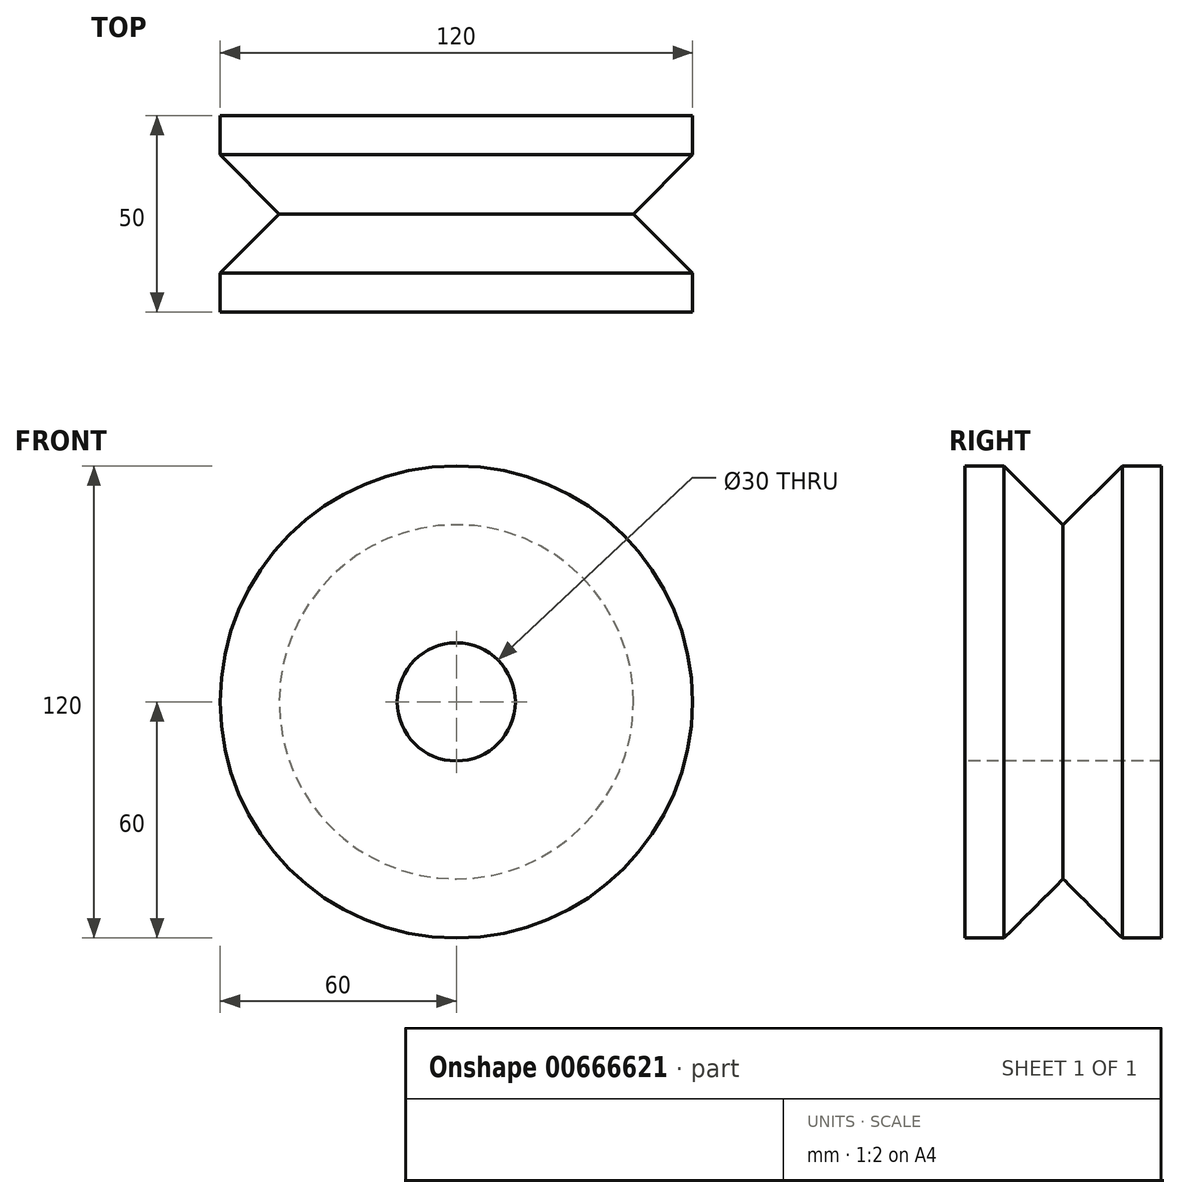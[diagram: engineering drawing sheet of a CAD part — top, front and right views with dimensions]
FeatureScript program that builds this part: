
annotation { "Feature Type Name" : "Feature", "Feature Type Description" : "" }
export const myFeature = defineFeature(function(context is Context, id is Id, definition is map)
    precondition{}
    {
        {
            var Q0;
            Q0=qCreatedBy(makeId("Right.planeOp"),FACE);
            var sketch = newSketch(context, id + "F0", { "sketchPlane" : qUnion([Q0])});
            skPoint(sketch, "E0.middle", {"position": v(0, 0) * mm});
            skLineSegment(sketch, "E1", {"start": v(0, 0) * mm, "end": v(15, 15) * mm});
            skLineSegment(sketch, "E2", {"start": v(0, 0) * mm, "end": v(-15, 15) * mm});
            skLineSegment(sketch, "E3", {"start": v(15, 15) * mm, "end": v(25, 15) * mm});
            skLineSegment(sketch, "E4", {"start": v(25, 15) * mm, "end": v(25, -45) * mm});
            skLineSegment(sketch, "E5", {"start": v(-15, 15) * mm, "end": v(-25, 15) * mm});
            skLineSegment(sketch, "E6", {"start": v(-25, 15) * mm, "end": v(-25, -45) * mm});
            skLineSegment(sketch, "E7", {"start": v(-25, -45) * mm, "end": v(25, -45) * mm});
            skSolve(sketch);
        }
        {
            var Q0;
            Q0=makeQuery(id+"F0.imprint","IMPRINT",FACE,{"disambiguationData":[TD([[makeQuery(id+"F0.imprint","IMPRINT",EDGE,{"derivedFrom":sQuery(id+"F0.wireOp",EDGE,"E1")}),-1.0]])]});
            var Q1;
            Q1=sQuery(id+"F0.wireOp",EDGE,"E7");
            revolve(context, id + "F1", {"surfaceOperationType" : NewSurfaceOperationType.NEW, "entities" : qUnion([Q0]), "axis" : qUnion([Q1]), "revolveType" : RevolveType.FULL});
        }
        {
            var Q0;
            Q0=makeQuery(id+"F1.opRevolve","SWEPT_FACE",FACE,{"disambiguationData":[OSD([sQuery(id+"F0.wireOp",EDGE,"E6")])]});
            var sketch = newSketch(context, id + "F2", { "sketchPlane" : qUnion([Q0])});
            skCircle(sketch, "E8", {"center": v(0, -45) * mm, "radius": 15 * mm});
            skSolve(sketch);
        }
        {
            var Q0;
            Q0=makeQuery(id+"F2.imprint","IMPRINT",FACE,{"disambiguationData":[TD([[makeQuery(id+"F2.imprint","IMPRINT",EDGE,{"derivedFrom":sQuery(id+"F2.wireOp",EDGE,"E8")}),1.0]])]});
            extrude(context, id + "F3", {"entities" : qUnion([Q0]), "operationType" : NewBodyOperationType.REMOVE, "oppositeDirection" : true, "depth" : 50 * mm, "offsetDistance" : 25 * mm});
        }
    });
